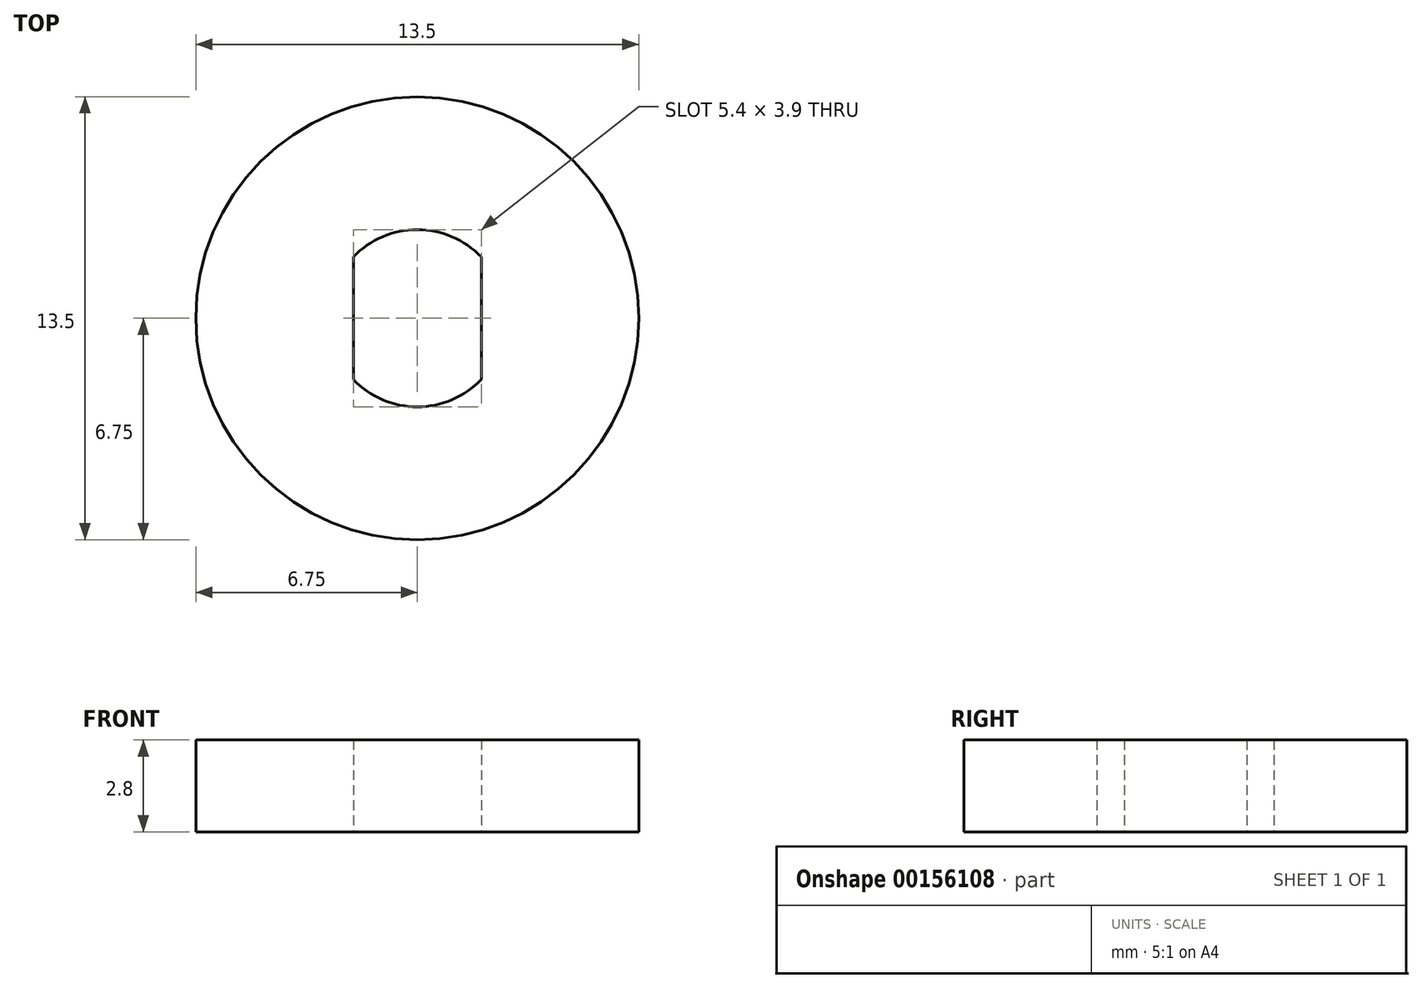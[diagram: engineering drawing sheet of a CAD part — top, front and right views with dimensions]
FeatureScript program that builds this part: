
annotation { "Feature Type Name" : "Feature", "Feature Type Description" : "" }
export const myFeature = defineFeature(function(context is Context, id is Id, definition is map)
    precondition{}
    {
        {
            var Q0;
            Q0=qCreatedBy(makeId("Top.planeOp"),FACE);
            var sketch = newSketch(context, id + "F0", { "sketchPlane" : qUnion([Q0])});
            skCircle(sketch, "E0", {"center": v(0, 0) * mm, "radius": 6.75 * mm});
            skArc(sketch, "E1", {"start": v(-1.95, -1.87) * mm, "mid": v(0, -2.7) * mm, "end": v(1.95, -1.87) * mm});
            skLineSegment(sketch, "E2", {"start": v(-1.95, 1.87) * mm, "end": v(-1.95, -1.87) * mm});
            skLineSegment(sketch, "E3", {"start": v(0, 8.65) * mm, "end": v(0, -8.33) * mm, "construction": true});
            skLineSegment(sketch, "E4.MirrorCS", {"start": v(1.95, 1.87) * mm, "end": v(1.95, -1.87) * mm});
            skArc(sketch, "E5.trimOffspring", {"start": v(1.95, 1.87) * mm, "mid": v(0, 2.7) * mm, "end": v(-1.95, 1.87) * mm});
            skSolve(sketch);
        }
        {
            var Q0;
            Q0=makeQuery(id+"F0.imprint","IMPRINT",FACE,{"disambiguationData":[TD([[makeQuery(id+"F0.imprint","IMPRINT",EDGE,{"derivedFrom":sQuery(id+"F0.wireOp",EDGE,"E0")}),1.0]])]});
            extrude(context, id + "F1", {"entities" : qUnion([Q0]), "depth" : 2.8 * mm});
        }
    });
